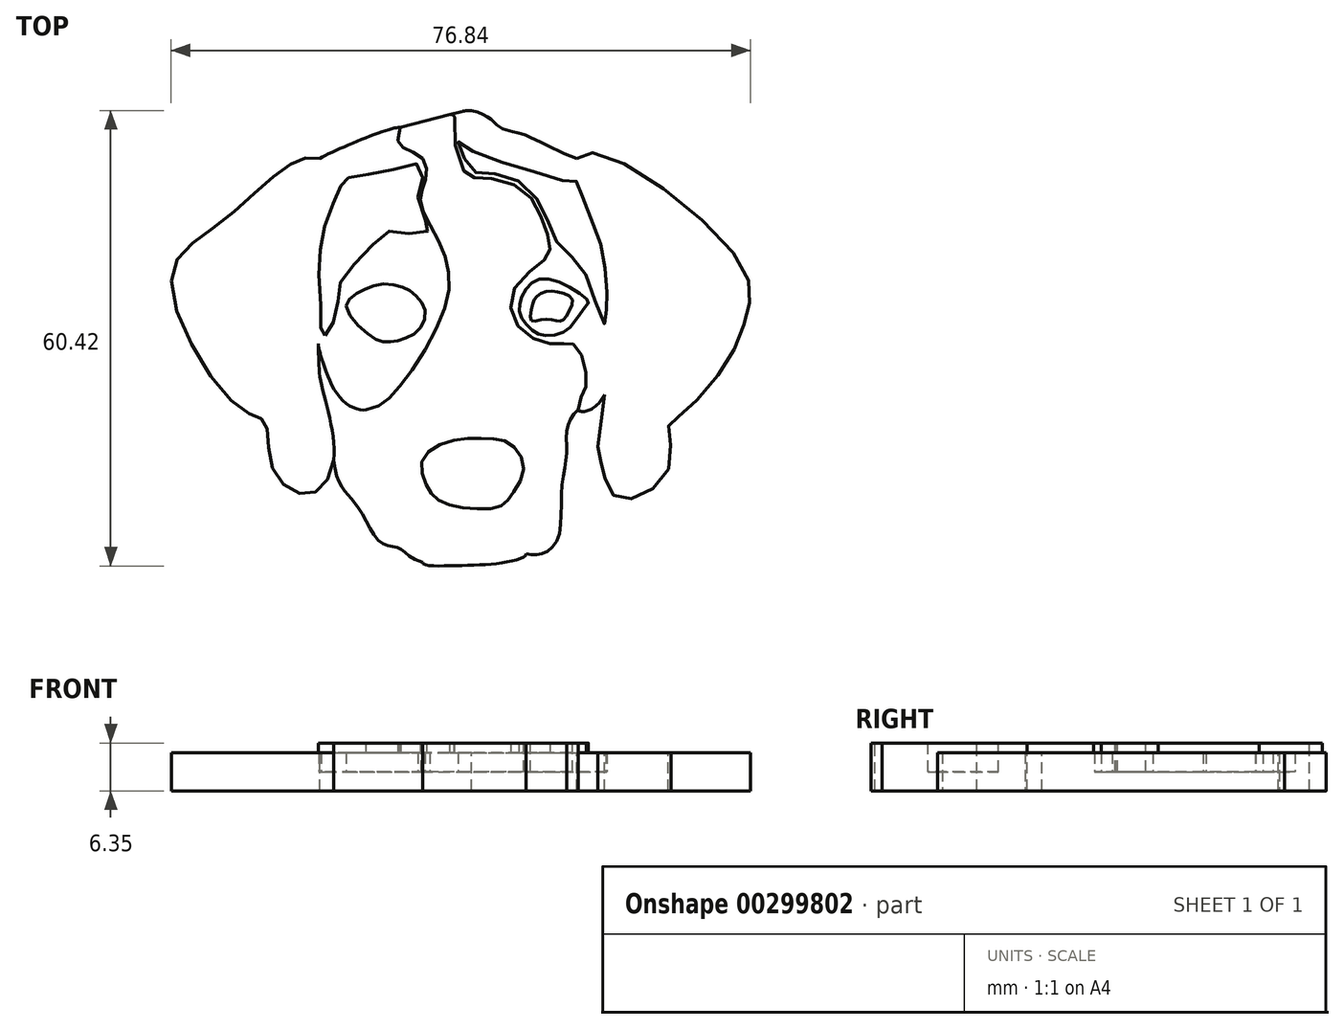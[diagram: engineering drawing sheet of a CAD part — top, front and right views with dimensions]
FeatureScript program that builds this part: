
annotation { "Feature Type Name" : "Feature", "Feature Type Description" : "" }
export const myFeature = defineFeature(function(context is Context, id is Id, definition is map)
    precondition{}
    {
        {
            var Q0;
            Q0=qCreatedBy(makeId("Top.planeOp"),FACE);
            var sketch = newSketch(context, id + "F0", { "sketchPlane" : qUnion([Q0])});
            skFitSpline(sketch, "E0", {"points": [v(-13.66, 27.6) * mm, v(-17.78, 26.67) * mm, v(-26.99, 18.92) * mm, v(-33.34, 11.59) * mm, v(-24.19, -5.58) * mm, v(-20.88, -7.44) * mm, v(-19.85, -13.65) * mm, v(-15.1, -16.96) * mm, v(-11.8, -12.41) * mm, v(-13.44, -2.27) * mm, v(-13.85, 2.98) * mm, v(-13.45, 18.91) * mm, v(-11.04, 25.53) * mm, v(-13.66, 27.6) * mm]});
            skFitSpline(sketch, "E1", {"points": [v(0, -25.98) * mm, v(3.57, -26.47) * mm, v(11.16, -25.98) * mm, v(13.75, -24.88) * mm, v(10.75, -22.95) * mm, v(6.62, -21.3) * mm, v(3.93, -22.74) * mm, v(0, -25.98) * mm]});
            skFitSpline(sketch, "E2", {"points": [v(23.24, -10.9) * mm, v(24.17, -3.78) * mm, v(23.78, 0) * mm, v(25.02, 13.65) * mm, v(20.47, 27.6) * mm, v(26.06, 27.2) * mm, v(42.53, 13.13) * mm, v(43.15, 7.35) * mm, v(40.44, 0.6) * mm, v(34.11, -6.54) * mm, v(32.64, -7.95) * mm, v(32.88, -12.87) * mm, v(28.45, -17.37) * mm, v(25.02, -16.8) * mm, v(23.78, -13.02) * mm, v(23.24, -10.9) * mm]});
            skFitSpline(sketch, "E3", {"points": [v(-13.66, 27.6) * mm, v(-2.96, 31.69) * mm, v(-3.17, 30.85) * mm, v(-2.86, 29.23) * mm, v(0, 27.6) * mm, v(0.34, 24.56) * mm, v(-0.27, 21.79) * mm, v(2.5, 15.8) * mm, v(3.07, 8.14) * mm, v(-3.5, -3.23) * mm, v(-7.45, -5.77) * mm], "startDerivative": vector(49.88, 27.02) * mm, "endDerivative": vector(-51.5, -11.1) * mm});
            skFitSpline(sketch, "E4", {"points": [v(-7.45, -5.77) * mm, v(-10.9, -4.19) * mm, v(-13.44, 1.24) * mm, v(-13.85, 2.98) * mm], "startDerivative": vector(-9.26, -1.19) * mm, "endDerivative": vector(-0.89, 6.86) * mm});
            skFitSpline(sketch, "E5", {"points": [v(6.53, 33.93) * mm, v(4.34, 33.05) * mm, v(5.76, 25.5) * mm, v(7.62, 25.06) * mm, v(13.32, 23.41) * mm, v(16.05, 19.03) * mm, v(16.93, 15.64) * mm, v(16.08, 14.05) * mm, v(12.22, 10.38) * mm, v(12.4, 5.78) * mm, v(16.08, 3.19) * mm, v(18.66, 2.98) * mm, v(19.89, 2.98) * mm, v(21.2, 1.24) * mm, v(21.75, -2.27) * mm, v(21.2, -3.75) * mm, v(20.65, -5.77) * mm, v(22.19, -5.77) * mm, v(24.17, -3.78) * mm], "startDerivative": vector(-56.64, 0.9) * mm, "endDerivative": vector(31.08, 53.1) * mm});
            skFitSpline(sketch, "E6", {"points": [v(6.53, 33.93) * mm, v(10.37, 31.69) * mm, v(13.2, 30.85) * mm, v(20.47, 27.6) * mm], "startDerivative": vector(20.86, -3.29) * mm, "endDerivative": vector(18.77, -6.28) * mm});
            skLineSegment(sketch, "E7", {"start": v(-2.96, 31.69) * mm, "end": v(5.26, 33.84) * mm});
            skFitSpline(sketch, "E8", {"points": [v(0, -25.98) * mm, v(-3.11, -24.12) * mm, v(-5.41, -23.46) * mm, v(-8.37, -18.97) * mm, v(-10.34, -16.56) * mm, v(-11.8, -12.41) * mm], "startDerivative": vector(-27.57, 6.34) * mm, "endDerivative": vector(-3.27, 28.64) * mm});
            skFitSpline(sketch, "E9", {"points": [v(13.75, -24.88) * mm, v(15.73, -24.88) * mm, v(17.92, -22.95) * mm, v(18.46, -16.45) * mm, v(19.12, -11.63) * mm, v(19.23, -8.02) * mm, v(20.65, -5.77) * mm], "startDerivative": vector(15.52, -2.17) * mm, "endDerivative": vector(13.18, 11.7) * mm});
            skFitSpline(sketch, "E10", {"points": [v(2.15, -17.77) * mm, v(0.52, -15.73) * mm, v(0, -12.4) * mm, v(3.62, -9.95) * mm, v(8.39, -9.56) * mm, v(11.64, -10.26) * mm, v(13.43, -13.39) * mm, v(11.9, -17) * mm, v(10.36, -18.53) * mm, v(6.3, -18.86) * mm, v(2.15, -17.77) * mm]});
            skFitSpline(sketch, "E11", {"points": [v(-8.57, 8.24) * mm, v(-7.53, 9.28) * mm, v(-5.74, 9.76) * mm, v(-4.01, 9.42) * mm, v(-2.9, 8.1) * mm, v(-2.84, 6.1) * mm, v(-4.01, 5.55) * mm, v(-6.08, 5.62) * mm, v(-7.8, 7.14) * mm, v(-8.57, 8.24) * mm]});
            skFitSpline(sketch, "E12", {"points": [v(14.44, 6.05) * mm, v(15.87, 6.21) * mm, v(17.51, 6.1) * mm, v(18.4, 6) * mm, v(19.16, 6.81) * mm, v(19.89, 8.84) * mm, v(18.4, 9.77) * mm, v(16.36, 9.94) * mm, v(15.05, 9.17) * mm, v(14.55, 7.96) * mm, v(14.44, 6.05) * mm]});
            skFitSpline(sketch, "E13", {"points": [v(-10.13, 8) * mm, v(-8.57, 9.74) * mm, v(-5.74, 10.87) * mm, v(-2.65, 10.52) * mm, v(-0.74, 9.28) * mm, v(0.36, 7.1) * mm, v(-0.75, 4.59) * mm, v(-3.14, 3.45) * mm, v(-5.08, 3.25) * mm, v(-7.25, 4.3) * mm, v(-10.13, 8) * mm]});
            skFitSpline(sketch, "E14", {"points": [v(12.9, 8.26) * mm, v(13.84, 10.38) * mm, v(15.89, 11.62) * mm, v(19.75, 10.38) * mm, v(22, 8.58) * mm, v(21.8, 8.13) * mm, v(20.4, 6.28) * mm, v(18.89, 4.6) * mm, v(16.14, 4.1) * mm, v(14.57, 4.8) * mm, v(13.1, 6.53) * mm, v(12.9, 8.26) * mm]});
            skFitSpline(sketch, "E15", {"points": [v(-12.92, 4.07) * mm, v(-12, 5.37) * mm, v(-11.2, 8.75) * mm, v(-10.7, 11.58) * mm, v(-7.39, 15.2) * mm, v(-4.56, 17.91) * mm, v(-1.6, 17.6) * mm, v(0.8, 17.98) * mm, v(0.93, 18.31) * mm, v(-0.57, 21.79) * mm, v(0, 24.99) * mm, v(-0.57, 26.82) * mm, v(-4.74, 25.84) * mm, v(-8.78, 25.33) * mm, v(-10.6, 24.56) * mm, v(-10.86, 23.85) * mm, v(-12.26, 20.72) * mm, v(-13.43, 16.42) * mm, v(-13.73, 11.59) * mm, v(-13.43, 5.63) * mm, v(-13.43, 4.37) * mm, v(-12.92, 4.07) * mm]});
            skFitSpline(sketch, "E16", {"points": [v(5.52, 27.6) * mm, v(4.74, 29.78) * mm, v(6.5, 28.65) * mm, v(13.77, 26.16) * mm, v(19.38, 24.56) * mm, v(20.4, 24.56) * mm, v(20.95, 23.33) * mm, v(23, 17.96) * mm, v(23.92, 15.13) * mm, v(24.46, 10.05) * mm, v(24.36, 8.25) * mm, v(24.27, 5.56) * mm, v(22.66, 9.42) * mm, v(20.85, 13.52) * mm, v(18.07, 16.1) * mm, v(16.75, 19.04) * mm, v(14.2, 23.43) * mm, v(10.06, 25.53) * mm, v(7.08, 25.72) * mm, v(5.52, 27.6) * mm]});
            skSolve(sketch);
        }
        {
            var Q0;
            Q0 = qSketchRegion(id + "F0", true);
            var Q1;
            Q1=makeQuery(id+"F0.imprint","IMPRINT",FACE,{"disambiguationData":[TD([[makeQuery(id+"F0.imprint","IMPRINT",EDGE,{"derivedFrom":sQuery(id+"F0.wireOp",EDGE,"E11")}),1.0]])]});
            var Q2;
            Q2=makeQuery(id+"F0.imprint","IMPRINT",FACE,{"disambiguationData":[TD([[makeQuery(id+"F0.imprint","IMPRINT",EDGE,{"derivedFrom":sQuery(id+"F0.wireOp",EDGE,"E15")}),1.0]])]});
            var Q3;
            Q3=makeQuery(id+"F0.imprint","IMPRINT",FACE,{"disambiguationData":[TD([[makeQuery(id+"F0.imprint","IMPRINT",EDGE,{"derivedFrom":sQuery(id+"F0.wireOp",EDGE,"E12")}),1.0]])]});
            var Q4;
            Q4=makeQuery(id+"F0.imprint","IMPRINT",FACE,{"disambiguationData":[TD([[makeQuery(id+"F0.imprint","IMPRINT",EDGE,{"derivedFrom":sQuery(id+"F0.wireOp",EDGE,"E12")}),-1.0]])]});
            var Q5;
            Q5=makeQuery(id+"F0.imprint","IMPRINT",FACE,{"disambiguationData":[TD([[makeQuery(id+"F0.imprint","IMPRINT",EDGE,{"derivedFrom":sQuery(id+"F0.wireOp",EDGE,"E16")}),-1.0]])]});
            var Q6;
            Q6=makeQuery(id+"F0.imprint","IMPRINT",FACE,{"disambiguationData":[TD([[makeQuery(id+"F0.imprint","IMPRINT",EDGE,{"derivedFrom":sQuery(id+"F0.wireOp",EDGE,"E11")}),-1.0]])]});
            var Q7;
            Q7=makeQuery(id+"F0.imprint","IMPRINT",FACE,{"disambiguationData":[TD([[makeQuery(id+"F0.imprint","IMPRINT",EDGE,{"derivedFrom":sQuery(id+"F0.wireOp",EDGE,"E10")}),-1.0]])]});
            extrude(context, id + "F1", {"entities" : qUnion([Q0, Q1, Q2, Q3, Q4, Q5, Q6, Q7]), "oppositeDirection" : true, "depth" : 6.35 * mm});
        }
        {
            var Q0;
            {var subQ0=sQuery(id+"F0.wireOp",EDGE,"E0");var subQ1=makeQuery(id+"F0.imprint","INTERSECT",VERTEX,{"derivedFrom":[subQ0,sQuery(id+"F0.wireOp",EDGE,"E3")]});Q0=makeQuery(id+"F0.imprint","IMPRINT",FACE,{"disambiguationData":[TD([[makeQuery(id+"F0.imprint","IMPRINT",EDGE,{"disambiguationData":[TD([[subQ1,-1.0]])],"derivedFrom":subQ0}),1.0]])]});}
            var Q1;
            {var subQ0=sQuery(id+"F0.wireOp",EDGE,"E4");Q1=makeQuery(id+"F0.imprint","IMPRINT",FACE,{"disambiguationData":[TD([[makeQuery(id+"F0.imprint","IMPRINT",EDGE,{"derivedFrom":subQ0}),-1.0]])]});}
            var Q2;
            {var subQ5=sQuery(id+"F0.wireOp",EDGE,"E6");Q2=makeQuery(id+"F0.imprint","IMPRINT",FACE,{"disambiguationData":[TD([[makeQuery(id+"F0.imprint","IMPRINT",EDGE,{"derivedFrom":subQ5}),-1.0]])]});}
            var Q3;
            {var subQ0=sQuery(id+"F0.wireOp",EDGE,"E2");var subQ1=makeQuery(id+"F0.imprint","INTERSECT",VERTEX,{"derivedFrom":[subQ0,sQuery(id+"F0.wireOp",EDGE,"E5")]});Q3=makeQuery(id+"F0.imprint","IMPRINT",FACE,{"disambiguationData":[TD([[makeQuery(id+"F0.imprint","IMPRINT",EDGE,{"disambiguationData":[TD([[subQ1,-1.0]])],"derivedFrom":subQ0}),-1.0]])]});}
            extrude(context, id + "F2", {"entities" : qUnion([Q0, Q1, Q2, Q3]), "operationType" : NewBodyOperationType.REMOVE, "oppositeDirection" : true, "depth" : 1.27 * mm});
        }
        {
            var Q0;
            Q0=makeQuery(id+"F0.imprint","IMPRINT",FACE,{"disambiguationData":[TD([[makeQuery(id+"F0.imprint","IMPRINT",EDGE,{"derivedFrom":sQuery(id+"F0.wireOp",EDGE,"E15")}),1.0]])]});
            var Q1;
            Q1=makeQuery(id+"F0.imprint","IMPRINT",FACE,{"disambiguationData":[TD([[makeQuery(id+"F0.imprint","IMPRINT",EDGE,{"derivedFrom":sQuery(id+"F0.wireOp",EDGE,"E11")}),-1.0]])]});
            var Q2;
            Q2=makeQuery(id+"F0.imprint","IMPRINT",FACE,{"disambiguationData":[TD([[makeQuery(id+"F0.imprint","IMPRINT",EDGE,{"derivedFrom":sQuery(id+"F0.wireOp",EDGE,"E11")}),1.0]])]});
            var Q3;
            Q3=makeQuery(id+"F0.imprint","IMPRINT",FACE,{"disambiguationData":[TD([[makeQuery(id+"F0.imprint","IMPRINT",EDGE,{"derivedFrom":sQuery(id+"F0.wireOp",EDGE,"E16")}),-1.0]])]});
            var Q4;
            Q4=makeQuery(id+"F0.imprint","IMPRINT",FACE,{"disambiguationData":[TD([[makeQuery(id+"F0.imprint","IMPRINT",EDGE,{"derivedFrom":sQuery(id+"F0.wireOp",EDGE,"E12")}),1.0]])]});
            var Q5;
            Q5=makeQuery(id+"F0.imprint","IMPRINT",FACE,{"disambiguationData":[TD([[makeQuery(id+"F0.imprint","IMPRINT",EDGE,{"derivedFrom":sQuery(id+"F0.wireOp",EDGE,"E10")}),-1.0]])]});
            extrude(context, id + "F3", {"entities" : qUnion([Q0, Q1, Q2, Q3, Q4, Q5]), "operationType" : NewBodyOperationType.REMOVE, "oppositeDirection" : true, "depth" : 3.8 * mm});
        }
        {
            var Q0;
            {var subQ0=sQuery(id+"F0.wireOp",EDGE,"E7");var subQ1=sQuery(id+"F0.wireOp",EDGE,"E5");Q0=makeQuery(id+"F2.boolean.opBoolean","SPLIT",EDGE,{"disambiguationData":[topologyDisambiguationEdgeConnected([makeQuery(id+"F2.opExtrude","SWEPT_FACE",FACE,{"disambiguationData":[OSD([subQ1])]})])],"derivedFrom":makeQuery(id+"F1.opExtrude","SWEPT_EDGE",EDGE,{"disambiguationData":[OSD([subQ1,subQ0])]})});}
            var Q1;
            {var subQ0=sQuery(id+"F0.wireOp",EDGE,"E7");var subQ1=sQuery(id+"F0.wireOp",EDGE,"E3");Q1=makeQuery(id+"F2.boolean.opBoolean","SPLIT",EDGE,{"disambiguationData":[topologyDisambiguationEdgeConnected([makeQuery(id+"F2.opExtrude","SWEPT_FACE",FACE,{"disambiguationData":[OSD([subQ1])]})])],"derivedFrom":makeQuery(id+"F1.opExtrude","SWEPT_EDGE",EDGE,{"disambiguationData":[OSD([subQ1,subQ0])]})});}
            fillet(context, id + "F4", {"entities" : qUnion([Q0, Q1]), "radius" : 0.5 * mm, "tangentPropagation" : true, "allowEdgeOverflow" : false});
        }
    });
